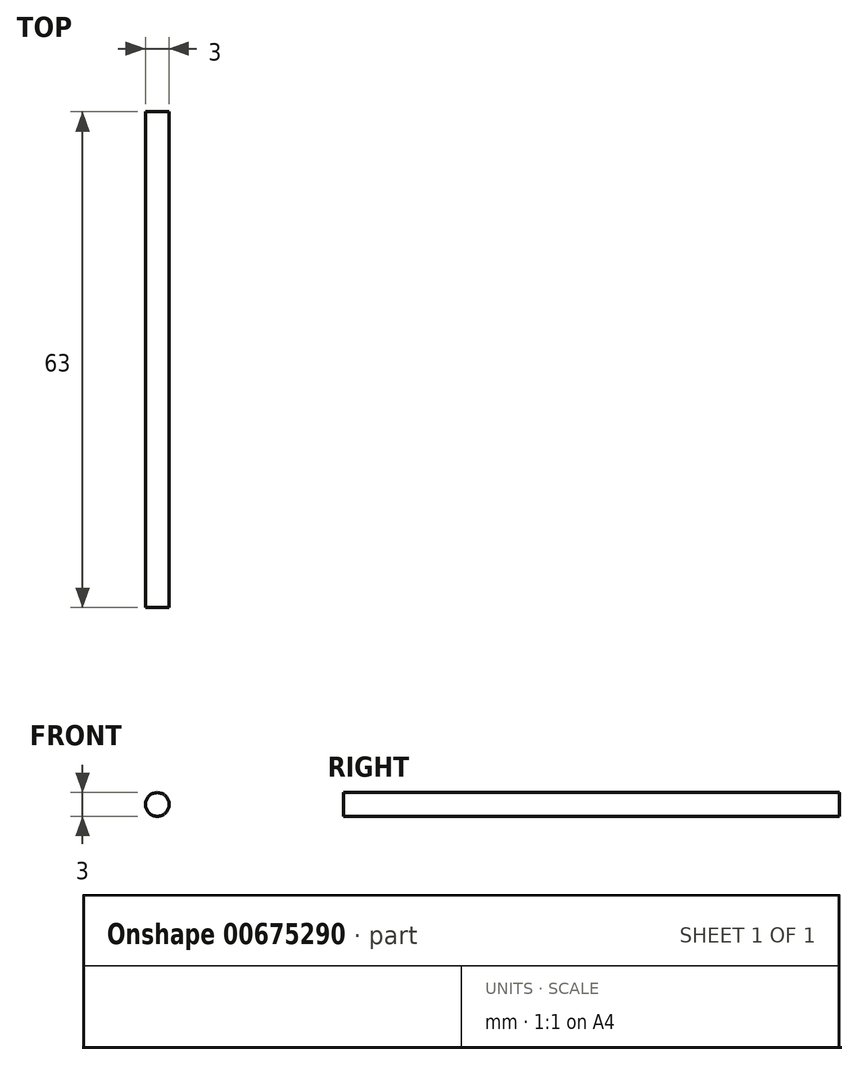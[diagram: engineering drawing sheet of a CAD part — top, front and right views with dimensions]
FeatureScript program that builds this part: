
annotation { "Feature Type Name" : "Feature", "Feature Type Description" : "" }
export const myFeature = defineFeature(function(context is Context, id is Id, definition is map)
    precondition{}
    {
        {
            var Q0;
            Q0=qCreatedBy(makeId("Front.planeOp"),FACE);
            var sketch = newSketch(context, id + "F0", { "sketchPlane" : qUnion([Q0])});
            skCircle(sketch, "E0", {"center": v(0, 0) * mm, "radius": 1.5 * mm});
            skSolve(sketch);
        }
        {
            var Q0;
            Q0 = qSketchRegion(id + "F0", true);
            extrude(context, id + "F1", {"entities" : qUnion([Q0]), "oppositeDirection" : true, "depth" : 63 * mm, "offsetDistance" : 25.4 * mm});
        }
    });
